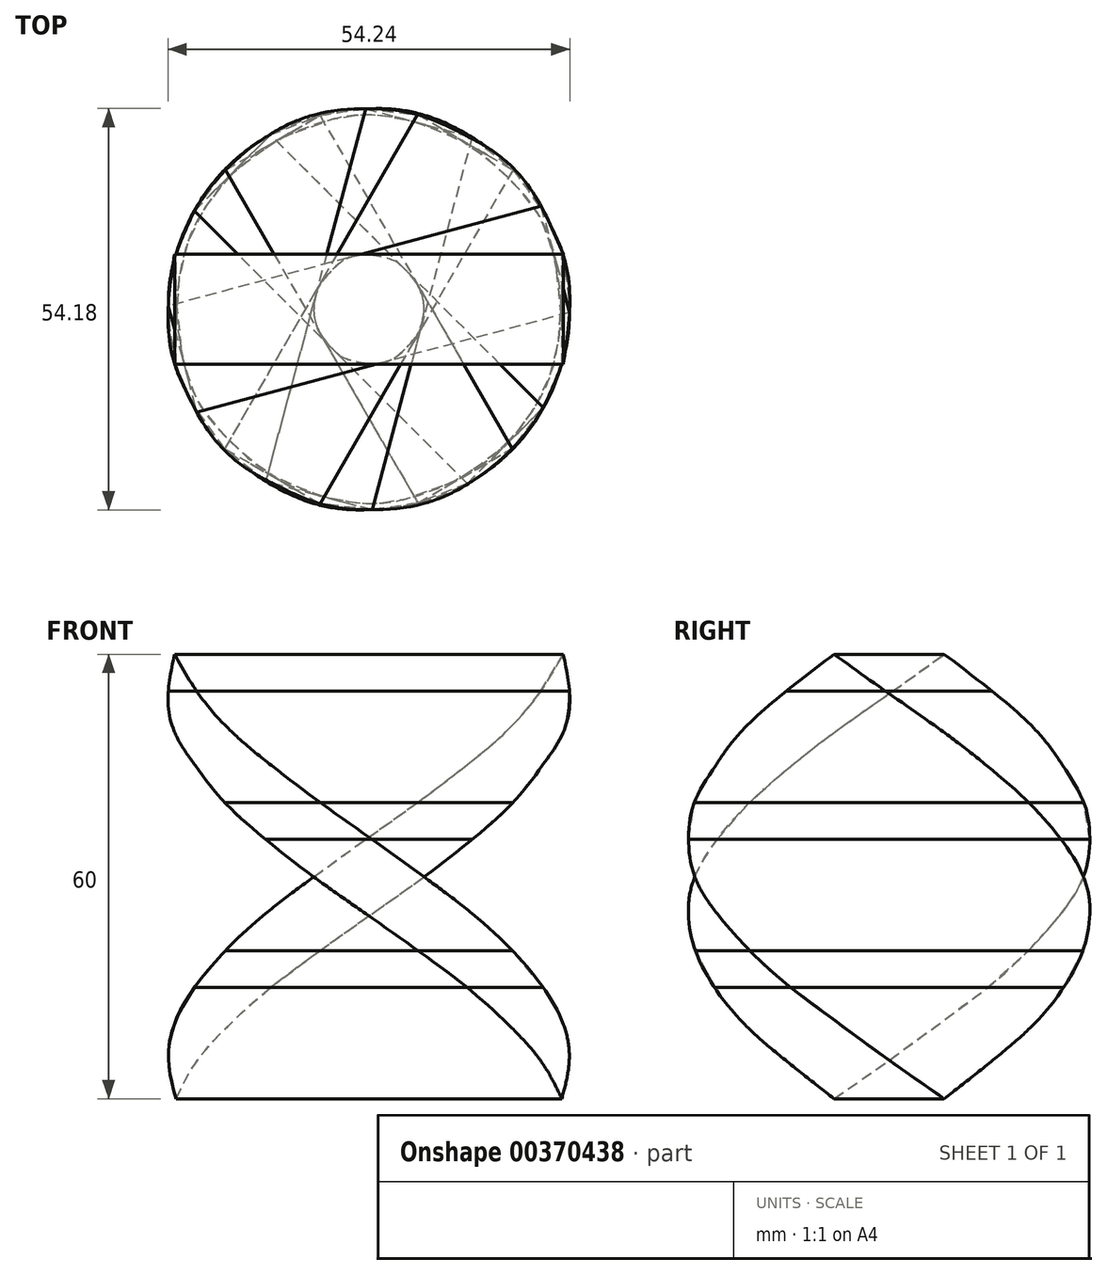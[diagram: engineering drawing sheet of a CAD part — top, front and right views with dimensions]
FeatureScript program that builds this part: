
annotation { "Feature Type Name" : "Feature", "Feature Type Description" : "" }
export const myFeature = defineFeature(function(context is Context, id is Id, definition is map)
    precondition{}
    {
        {
            var Q0;
            Q0=qCreatedBy(makeId("Top.planeOp"),FACE);
            cPlane(context, id + "F0", {"entities" : qUnion([Q0]), "cplaneType" : CPlaneType.OFFSET, "offset" : 5 * mm, "width" : 152.4 * mm, "height" : 152.4 * mm});
        }
        {
            var Q0;
            Q0=qCreatedBy(id+"F0.planeOp",FACE);
            var sketch = newSketch(context, id + "F1", { "sketchPlane" : qUnion([Q0])});
            skLineSegment(sketch, "E0.bottom", {"start": v(-26.04, -7.44) * mm, "end": v(26.04, -7.44) * mm});
            skLineSegment(sketch, "E0.top", {"start": v(-26.04, 7.44) * mm, "end": v(26.04, 7.44) * mm});
            skLineSegment(sketch, "E0.left", {"start": v(-26.04, -7.44) * mm, "end": v(-26.04, 7.44) * mm});
            skLineSegment(sketch, "E0.right", {"start": v(26.04, -7.44) * mm, "end": v(26.04, 7.44) * mm});
            skPoint(sketch, "E0.middle", {"position": v(0, 0) * mm});
            skSolve(sketch);
        }
        {
            var Q0;
            Q0=qCreatedBy(id+"F0.planeOp",FACE);
            cPlane(context, id + "F2", {"entities" : qUnion([Q0]), "cplaneType" : CPlaneType.OFFSET, "offset" : 5 * mm, "width" : 152.4 * mm, "height" : 152.4 * mm});
        }
        {
            var Q0;
            Q0=qCreatedBy(id+"F2.planeOp",FACE);
            var sketch = newSketch(context, id + "F3", { "sketchPlane" : qUnion([Q0])});
            skLineSegment(sketch, "E1.bottom", {"start": v(-27.03, -0.27) * mm, "end": v(23.27, -13.75) * mm});
            skLineSegment(sketch, "E1.top", {"start": v(-23.27, 13.75) * mm, "end": v(27.03, 0.27) * mm});
            skLineSegment(sketch, "E1.left", {"start": v(-27.03, -0.27) * mm, "end": v(-23.27, 13.75) * mm});
            skLineSegment(sketch, "E1.right", {"start": v(23.27, -13.75) * mm, "end": v(27.03, 0.27) * mm});
            skPoint(sketch, "E1.middle", {"position": v(0, 0) * mm});
            skSolve(sketch);
        }
        {
            var Q0;
            Q0=qCreatedBy(id+"F2.planeOp",FACE);
            cPlane(context, id + "F4", {"entities" : qUnion([Q0]), "cplaneType" : CPlaneType.OFFSET, "offset" : 5 * mm, "width" : 152.4 * mm, "height" : 152.4 * mm});
        }
        {
            var Q0;
            Q0=qCreatedBy(id+"F4.planeOp",FACE);
            var sketch = newSketch(context, id + "F5", { "sketchPlane" : qUnion([Q0])});
            skLineSegment(sketch, "E2.bottom", {"start": v(-26.27, 6.58) * mm, "end": v(18.83, -19.46) * mm});
            skLineSegment(sketch, "E2.top", {"start": v(-18.83, 19.46) * mm, "end": v(26.27, -6.58) * mm});
            skLineSegment(sketch, "E2.left", {"start": v(-26.27, 6.58) * mm, "end": v(-18.83, 19.46) * mm});
            skLineSegment(sketch, "E2.right", {"start": v(18.83, -19.46) * mm, "end": v(26.27, -6.58) * mm});
            skPoint(sketch, "E2.middle", {"position": v(0, 0) * mm});
            skSolve(sketch);
        }
        {
            var Q0;
            Q0=qCreatedBy(id+"F4.planeOp",FACE);
            cPlane(context, id + "F6", {"entities" : qUnion([Q0]), "cplaneType" : CPlaneType.OFFSET, "offset" : 5 * mm, "width" : 152.4 * mm, "height" : 152.4 * mm});
        }
        {
            var Q0;
            Q0=qCreatedBy(id+"F6.planeOp",FACE);
            var sketch = newSketch(context, id + "F7", { "sketchPlane" : qUnion([Q0])});
            skLineSegment(sketch, "E3.bottom", {"start": v(13.28, -23.54) * mm, "end": v(-23.54, 13.28) * mm});
            skLineSegment(sketch, "E3.top", {"start": v(23.54, -13.28) * mm, "end": v(-13.28, 23.54) * mm});
            skLineSegment(sketch, "E3.left", {"start": v(13.28, -23.54) * mm, "end": v(23.54, -13.28) * mm});
            skLineSegment(sketch, "E3.right", {"start": v(-23.54, 13.28) * mm, "end": v(-13.28, 23.54) * mm});
            skPoint(sketch, "E3.middle", {"position": v(0, 0) * mm});
            skSolve(sketch);
        }
        {
            var Q0;
            Q0=qCreatedBy(id+"F6.planeOp",FACE);
            cPlane(context, id + "F8", {"entities" : qUnion([Q0]), "cplaneType" : CPlaneType.OFFSET, "offset" : 5 * mm, "width" : 152.4 * mm, "height" : 152.4 * mm});
        }
        {
            var Q0;
            Q0=qCreatedBy(id+"F8.planeOp",FACE);
            var sketch = newSketch(context, id + "F9", { "sketchPlane" : qUnion([Q0])});
            skPoint(sketch, "E4.middle", {"position": v(0, 0) * mm});
            skLineSegment(sketch, "E5.bottom", {"start": v(-19.35, 18.8) * mm, "end": v(6.6, -26.15) * mm});
            skLineSegment(sketch, "E5.top", {"start": v(-6.6, 26.15) * mm, "end": v(19.35, -18.8) * mm});
            skLineSegment(sketch, "E5.left", {"start": v(-19.35, 18.8) * mm, "end": v(-6.6, 26.15) * mm});
            skLineSegment(sketch, "E5.right", {"start": v(6.6, -26.15) * mm, "end": v(19.35, -18.8) * mm});
            skSolve(sketch);
        }
        {
            var Q0;
            Q0=qCreatedBy(id+"F8.planeOp",FACE);
            cPlane(context, id + "F10", {"entities" : qUnion([Q0]), "cplaneType" : CPlaneType.OFFSET, "offset" : 5 * mm, "width" : 152.4 * mm, "height" : 152.4 * mm});
        }
        {
            var Q0;
            Q0=qCreatedBy(id+"F10.planeOp",FACE);
            var sketch = newSketch(context, id + "F11", { "sketchPlane" : qUnion([Q0])});
            skLineSegment(sketch, "E6.bottom", {"start": v(-13.92, 23.22) * mm, "end": v(-0.45, -27.07) * mm});
            skLineSegment(sketch, "E6.top", {"start": v(0.45, 27.07) * mm, "end": v(13.92, -23.22) * mm});
            skLineSegment(sketch, "E6.left", {"start": v(-13.92, 23.22) * mm, "end": v(0.45, 27.07) * mm});
            skLineSegment(sketch, "E6.right", {"start": v(-0.45, -27.07) * mm, "end": v(13.92, -23.22) * mm});
            skPoint(sketch, "E6.middle", {"position": v(0, 0) * mm});
            skSolve(sketch);
        }
        {
            var Q0;
            Q0=qCreatedBy(id+"F10.planeOp",FACE);
            cPlane(context, id + "F12", {"entities" : qUnion([Q0]), "cplaneType" : CPlaneType.OFFSET, "offset" : 5 * mm, "width" : 152.4 * mm, "height" : 152.4 * mm});
        }
        {
            var Q0;
            Q0=qCreatedBy(id+"F12.planeOp",FACE);
            var sketch = newSketch(context, id + "F13", { "sketchPlane" : qUnion([Q0])});
            skLineSegment(sketch, "E7.bottom", {"start": v(-7.37, 26.24) * mm, "end": v(-7.51, -26.2) * mm});
            skLineSegment(sketch, "E7.top", {"start": v(7.51, 26.2) * mm, "end": v(7.37, -26.24) * mm});
            skLineSegment(sketch, "E7.left", {"start": v(-7.37, 26.24) * mm, "end": v(7.51, 26.2) * mm});
            skLineSegment(sketch, "E7.right", {"start": v(-7.51, -26.2) * mm, "end": v(7.37, -26.24) * mm});
            skPoint(sketch, "E7.middle", {"position": v(0, 0) * mm});
            skSolve(sketch);
        }
        {
            var Q0;
            Q0=qCreatedBy(id+"F12.planeOp",FACE);
            cPlane(context, id + "F14", {"entities" : qUnion([Q0]), "cplaneType" : CPlaneType.OFFSET, "offset" : 5 * mm, "width" : 152.4 * mm, "height" : 152.4 * mm});
        }
        {
            var Q0;
            Q0=qCreatedBy(id+"F14.planeOp",FACE);
            var sketch = newSketch(context, id + "F15", { "sketchPlane" : qUnion([Q0])});
            skLineSegment(sketch, "E8.bottom", {"start": v(-0.45, 27.07) * mm, "end": v(-13.92, -23.22) * mm});
            skLineSegment(sketch, "E8.top", {"start": v(13.92, 23.22) * mm, "end": v(0.45, -27.07) * mm});
            skLineSegment(sketch, "E8.left", {"start": v(-0.45, 27.07) * mm, "end": v(13.92, 23.22) * mm});
            skLineSegment(sketch, "E8.right", {"start": v(-13.92, -23.22) * mm, "end": v(0.45, -27.07) * mm});
            skPoint(sketch, "E8.middle", {"position": v(0, 0) * mm});
            skSolve(sketch);
        }
        {
            var Q0;
            Q0=qCreatedBy(id+"F14.planeOp",FACE);
            cPlane(context, id + "F16", {"entities" : qUnion([Q0]), "cplaneType" : CPlaneType.OFFSET, "offset" : 5 * mm, "width" : 152.4 * mm, "height" : 152.4 * mm});
        }
        {
            var Q0;
            Q0=qCreatedBy(id+"F16.planeOp",FACE);
            var sketch = newSketch(context, id + "F17", { "sketchPlane" : qUnion([Q0])});
            skLineSegment(sketch, "E9.bottom", {"start": v(6.58, 26.27) * mm, "end": v(-19.46, -18.83) * mm});
            skLineSegment(sketch, "E9.top", {"start": v(19.46, 18.83) * mm, "end": v(-6.58, -26.27) * mm});
            skLineSegment(sketch, "E9.left", {"start": v(6.58, 26.27) * mm, "end": v(19.46, 18.83) * mm});
            skLineSegment(sketch, "E9.right", {"start": v(-19.46, -18.83) * mm, "end": v(-6.58, -26.27) * mm});
            skPoint(sketch, "E9.middle", {"position": v(0, 0) * mm});
            skSolve(sketch);
        }
        {
            var Q0;
            Q0=qCreatedBy(id+"F16.planeOp",FACE);
            cPlane(context, id + "F18", {"entities" : qUnion([Q0]), "cplaneType" : CPlaneType.OFFSET, "offset" : 5 * mm, "width" : 152.4 * mm, "height" : 152.4 * mm});
        }
        {
            var Q0;
            Q0=qCreatedBy(id+"F18.planeOp",FACE);
            var sketch = newSketch(context, id + "F19", { "sketchPlane" : qUnion([Q0])});
            skLineSegment(sketch, "E10.bottom", {"start": v(13.15, 23.41) * mm, "end": v(-23.41, -13.15) * mm});
            skLineSegment(sketch, "E10.top", {"start": v(23.41, 13.15) * mm, "end": v(-13.15, -23.41) * mm});
            skLineSegment(sketch, "E10.left", {"start": v(13.15, 23.41) * mm, "end": v(23.41, 13.15) * mm});
            skLineSegment(sketch, "E10.right", {"start": v(-23.41, -13.15) * mm, "end": v(-13.15, -23.41) * mm});
            skPoint(sketch, "E10.middle", {"position": v(0, 0) * mm});
            skSolve(sketch);
        }
        {
            var Q0;
            Q0=qCreatedBy(id+"F18.planeOp",FACE);
            cPlane(context, id + "F20", {"entities" : qUnion([Q0]), "cplaneType" : CPlaneType.OFFSET, "offset" : 5 * mm, "width" : 152.4 * mm, "height" : 152.4 * mm});
        }
        {
            var Q0;
            Q0=qCreatedBy(id+"F20.planeOp",FACE);
            var sketch = newSketch(context, id + "F21", { "sketchPlane" : qUnion([Q0])});
            skLineSegment(sketch, "E11.bottom", {"start": v(18.98, 19.55) * mm, "end": v(-26.42, -6.67) * mm});
            skLineSegment(sketch, "E11.top", {"start": v(26.42, 6.67) * mm, "end": v(-18.98, -19.55) * mm});
            skLineSegment(sketch, "E11.left", {"start": v(18.98, 19.55) * mm, "end": v(26.42, 6.67) * mm});
            skLineSegment(sketch, "E11.right", {"start": v(-26.42, -6.67) * mm, "end": v(-18.98, -19.55) * mm});
            skPoint(sketch, "E11.middle", {"position": v(0, 0) * mm});
            skSolve(sketch);
        }
        {
            var Q0;
            Q0=qCreatedBy(id+"F20.planeOp",FACE);
            cPlane(context, id + "F22", {"entities" : qUnion([Q0]), "cplaneType" : CPlaneType.OFFSET, "offset" : 5 * mm, "width" : 152.4 * mm, "height" : 152.4 * mm});
        }
        {
            var Q0;
            Q0=qCreatedBy(id+"F22.planeOp",FACE);
            var sketch = newSketch(context, id + "F23", { "sketchPlane" : qUnion([Q0])});
            skLineSegment(sketch, "E12.bottom", {"start": v(23.22, 13.92) * mm, "end": v(-27.07, 0.45) * mm});
            skLineSegment(sketch, "E12.top", {"start": v(27.07, -0.45) * mm, "end": v(-23.22, -13.92) * mm});
            skLineSegment(sketch, "E12.left", {"start": v(23.22, 13.92) * mm, "end": v(27.07, -0.45) * mm});
            skLineSegment(sketch, "E12.right", {"start": v(-27.07, 0.45) * mm, "end": v(-23.22, -13.92) * mm});
            skPoint(sketch, "E12.middle", {"position": v(0, 0) * mm});
            skSolve(sketch);
        }
        {
            var Q0;
            Q0=qCreatedBy(id+"F22.planeOp",FACE);
            cPlane(context, id + "F24", {"entities" : qUnion([Q0]), "cplaneType" : CPlaneType.OFFSET, "offset" : 5 * mm, "width" : 152.4 * mm, "height" : 152.4 * mm});
        }
        {
            var Q0;
            Q0=qCreatedBy(id+"F24.planeOp",FACE);
            var sketch = newSketch(context, id + "F25", { "sketchPlane" : qUnion([Q0])});
            skLineSegment(sketch, "E13.bottom", {"start": v(26.22, 7.44) * mm, "end": v(-26.22, 7.44) * mm});
            skLineSegment(sketch, "E13.top", {"start": v(26.22, -7.44) * mm, "end": v(-26.22, -7.44) * mm});
            skLineSegment(sketch, "E13.left", {"start": v(26.22, 7.44) * mm, "end": v(26.22, -7.44) * mm});
            skLineSegment(sketch, "E13.right", {"start": v(-26.22, 7.44) * mm, "end": v(-26.22, -7.44) * mm});
            skPoint(sketch, "E13.middle", {"position": v(0, 0) * mm});
            skSolve(sketch);
        }
        {
            var Q0;
            Q0 = qSketchRegion(id + "F1", true);
            var Q1;
            Q1 = qSketchRegion(id + "F3", true);
            var Q2;
            Q2 = qSketchRegion(id + "F5", true);
            var Q3;
            Q3 = qSketchRegion(id + "F7", true);
            loft(context, id + "F26", {"sheetProfilesArray" : [{ "sheetProfileEntities" : qUnion([Q0]) }, { "sheetProfileEntities" : qUnion([Q1]) }, { "sheetProfileEntities" : qUnion([Q2]) }, { "sheetProfileEntities" : qUnion([Q3]) }]});
        }
        {
            var Q0;
            Q0 = qSketchRegion(id + "F9", true);
            var Q1;
            Q1 = qSketchRegion(id + "F11", true);
            var Q2;
            Q2 = qSketchRegion(id + "F13", true);
            var Q3;
            Q3 = qSketchRegion(id + "F15", true);
            loft(context, id + "F27", {"sheetProfilesArray" : [{ "sheetProfileEntities" : qUnion([Q0]) }, { "sheetProfileEntities" : qUnion([Q1]) }, { "sheetProfileEntities" : qUnion([Q2]) }, { "sheetProfileEntities" : qUnion([Q3]) }]});
        }
        {
            var Q0;
            Q0 = qSketchRegion(id + "F7", true);
            var Q1;
            Q1 = qSketchRegion(id + "F9", true);
            loft(context, id + "F28", {"sheetProfilesArray" : [{ "sheetProfileEntities" : qUnion([Q0]) }, { "sheetProfileEntities" : qUnion([Q1]) }]});
        }
        {
            var Q0;
            Q0 = qSketchRegion(id + "F17", true);
            var Q1;
            Q1 = qSketchRegion(id + "F19", true);
            var Q2;
            Q2 = qSketchRegion(id + "F21", true);
            var Q3;
            Q3 = qSketchRegion(id + "F23", true);
            loft(context, id + "F29", {"sheetProfilesArray" : [{ "sheetProfileEntities" : qUnion([Q0]) }, { "sheetProfileEntities" : qUnion([Q1]) }, { "sheetProfileEntities" : qUnion([Q2]) }, { "sheetProfileEntities" : qUnion([Q3]) }]});
        }
        {
            var Q0;
            Q0 = qSketchRegion(id + "F15", true);
            var Q1;
            Q1 = qSketchRegion(id + "F17", true);
            loft(context, id + "F30", {"sheetProfilesArray" : [{ "sheetProfileEntities" : qUnion([Q0]) }, { "sheetProfileEntities" : qUnion([Q1]) }]});
        }
        {
            var Q1;
            Q1 = qSketchRegion(id + "F23", true);
            var Q2;
            Q2 = qSketchRegion(id + "F25", true);
            loft(context, id + "F31", {"operationType" : NewBodyOperationType.ADD, "sheetProfilesArray" : [{ "sheetProfileEntities" : qUnion([Q1]) }, { "sheetProfileEntities" : qUnion([Q2]) }]});
        }
        {
            var Q0;
            Q0 = qSketchRegion(id + "F1", true);
            var Q1;
            Q1 = qSketchRegion(id + "F3", true);
            var Q2;
            Q2 = qSketchRegion(id + "F5", true);
            var Q3;
            Q3 = qSketchRegion(id + "F7", true);
            var Q4;
            Q4 = qSketchRegion(id + "F9", true);
            var Q5;
            Q5 = qSketchRegion(id + "F11", true);
            var Q6;
            Q6 = qSketchRegion(id + "F13", true);
            var Q7;
            Q7 = qSketchRegion(id + "F15", true);
            var Q8;
            Q8 = qSketchRegion(id + "F17", true);
            var Q9;
            Q9 = qSketchRegion(id + "F19", true);
            var Q10;
            Q10 = qSketchRegion(id + "F21", true);
            var Q11;
            Q11 = qSketchRegion(id + "F23", true);
            var Q12;
            Q12 = qSketchRegion(id + "F25", true);
            loft(context, id + "F32", {"sheetProfilesArray" : [{ "sheetProfileEntities" : qUnion([Q0]) }, { "sheetProfileEntities" : qUnion([Q1]) }, { "sheetProfileEntities" : qUnion([Q2]) }, { "sheetProfileEntities" : qUnion([Q3]) }, { "sheetProfileEntities" : qUnion([Q4]) }, { "sheetProfileEntities" : qUnion([Q5]) }, { "sheetProfileEntities" : qUnion([Q6]) }, { "sheetProfileEntities" : qUnion([Q7]) }, { "sheetProfileEntities" : qUnion([Q8]) }, { "sheetProfileEntities" : qUnion([Q9]) }, { "sheetProfileEntities" : qUnion([Q10]) }, { "sheetProfileEntities" : qUnion([Q11]) }, { "sheetProfileEntities" : qUnion([Q12]) }]});
        }
    });
